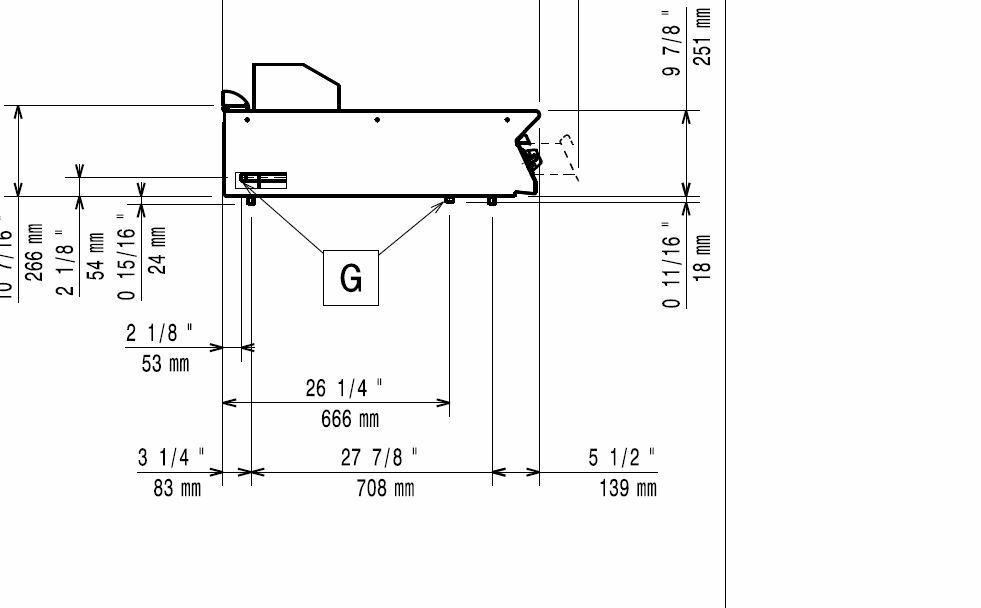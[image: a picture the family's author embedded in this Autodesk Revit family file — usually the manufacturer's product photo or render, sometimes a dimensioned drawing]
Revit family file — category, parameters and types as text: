
# Revit family: QF_ELECTROLUXPROFESSIONAL_391591_E9IIMTAOMEI
name_source: partatom
category: Attrezzature speciali
revit_build: Autodesk Revit 2018 (Build: 20181011_1500(x64)
units: mm (PartAtom-declared; Revit-internal decimal feet)

## family parameters
Basato su piano di lavoro = No
Condiviso = No
Punto di calcolo locali = No
Quota connettore circolare = Usa diametro
Sempre verticale = Sì
Taglio con vuoti quando caricato = No
Tipo di parte = Normale

## types (1)
- Standard
    Accessory = Sì
    Cold Water Size = 0"
    Compressed Air Pressure = 0.00 psi
    Compressed Air Size = 0"
    Compressed Air Volume = 0 GPM
    Condensate Return Size = 0"
    Cycle = 0 Hz
    Depth Actual = 930 mm
    Descrizione = GAS FRY TOP SMOOTH+RIBBED SLOPED PLATE.800MM-BRUSHED CHROME - QMARK
    Direct Waste Size = 0"
    Gas Input Pressure = 0.7
    Gas KW = 20
    Gas Size = 1"
    HP = 0 HP
    Height Actual = 250 mm  [stored 0.82021 ft]
    Hot Water Size = 0"
    Item Number = 391591
    Length Actual = 800 mm  [stored 2.62467 ft]
    Modello = E9IIMTAOMEI
    Phase = 0
    Produttore = Electrolux Professional
    Refrigerant Compressor Remote = Sì
    Refrigeration Liquid Line Size = 0 mm  [stored 0 ft]
    Refrigeration Suction Line Size = 0 mm  [stored 0 ft]
    Steam Consumption per Hour = 0
    Steam Supply Maximum Pressure = 0.00 psi
    Steam Supply Minimum Pressure = 0.00 psi
    Steam Supply Size = 0"
    URL = https://www.electroluxprofessional.com
    URL Manufacturer = https://www.electroluxprofessional.com
    Volts = 0 V
    Watts = 0 W
    Weight = 105.00 kg

note: source unit labels omitted for Gas Input Pressure — the stored unit's dimension contradicts the parameter name (converter mislabeling)

note: [stored X ft] marks values corroborated as IEEE doubles in the binary element streams (Revit-internal decimal feet)

## geometry (parser evidence)
native form markers: Blend x28, Sweep x2
no freeform markers — native parametric forms only
